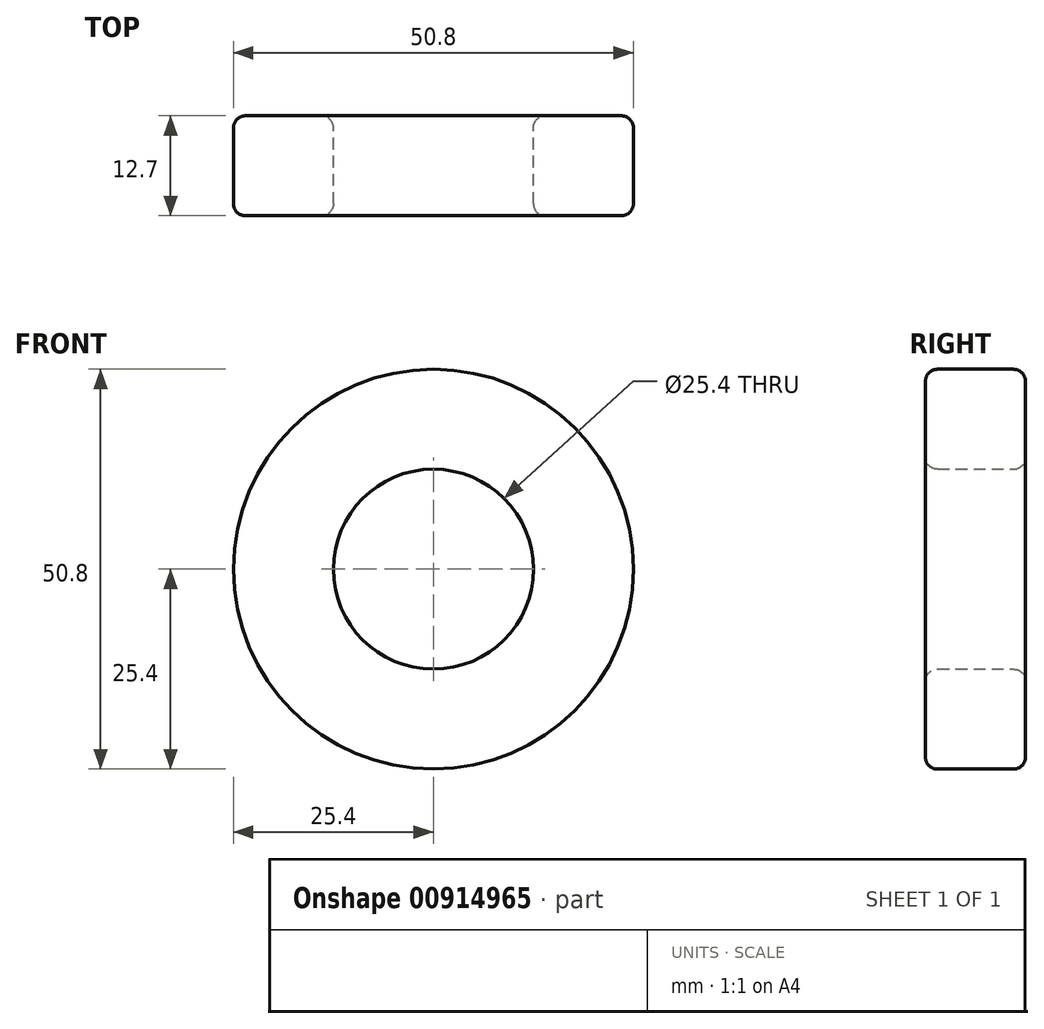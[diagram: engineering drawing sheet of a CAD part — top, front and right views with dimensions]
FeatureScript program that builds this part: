
annotation { "Feature Type Name" : "Feature", "Feature Type Description" : "" }
export const myFeature = defineFeature(function(context is Context, id is Id, definition is map)
    precondition{}
    {
        {
            var Q0;
            Q0=qCreatedBy(makeId("Front.planeOp"),FACE);
            var sketch = newSketch(context, id + "F0", { "sketchPlane" : qUnion([Q0])});
            skCircle(sketch, "E0", {"center": v(0, 0) * mm, "radius": 12.7 * mm});
            skCircle(sketch, "E1", {"center": v(0, 0) * mm, "radius": 25.4 * mm});
            skSolve(sketch);
        }
        {
            var Q0;
            Q0 = qSketchRegion(id + "F0", true);
            extrude(context, id + "F1", {"entities" : qUnion([Q0]), "depth" : 12.7 * mm, "offsetDistance" : 25.4 * mm});
        }
        {
            var Q0;
            Q0=makeQuery(id+"F1.opExtrude","CAP_EDGE",EDGE,{"disambiguationData":[OSD([sQuery(id+"F0.wireOp",EDGE,"E0")])],"isStart":false});
            var Q1;
            Q1=makeQuery(id+"F1.opExtrude","CAP_EDGE",EDGE,{"disambiguationData":[OSD([sQuery(id+"F0.wireOp",EDGE,"E1")])],"isStart":false});
            var Q2;
            Q2=makeQuery(id+"F1.opExtrude","CAP_EDGE",EDGE,{"disambiguationData":[OSD([sQuery(id+"F0.wireOp",EDGE,"E1")])],"isStart":true});
            var Q3;
            Q3=makeQuery(id+"F1.opExtrude","CAP_EDGE",EDGE,{"disambiguationData":[OSD([sQuery(id+"F0.wireOp",EDGE,"E0")])],"isStart":true});
            fillet(context, id + "F2", {"entities" : qUnion([Q0, Q1, Q2, Q3]), "radius" : 1.52 * mm, "tangentPropagation" : true, "allowEdgeOverflow" : false});
        }
    });
